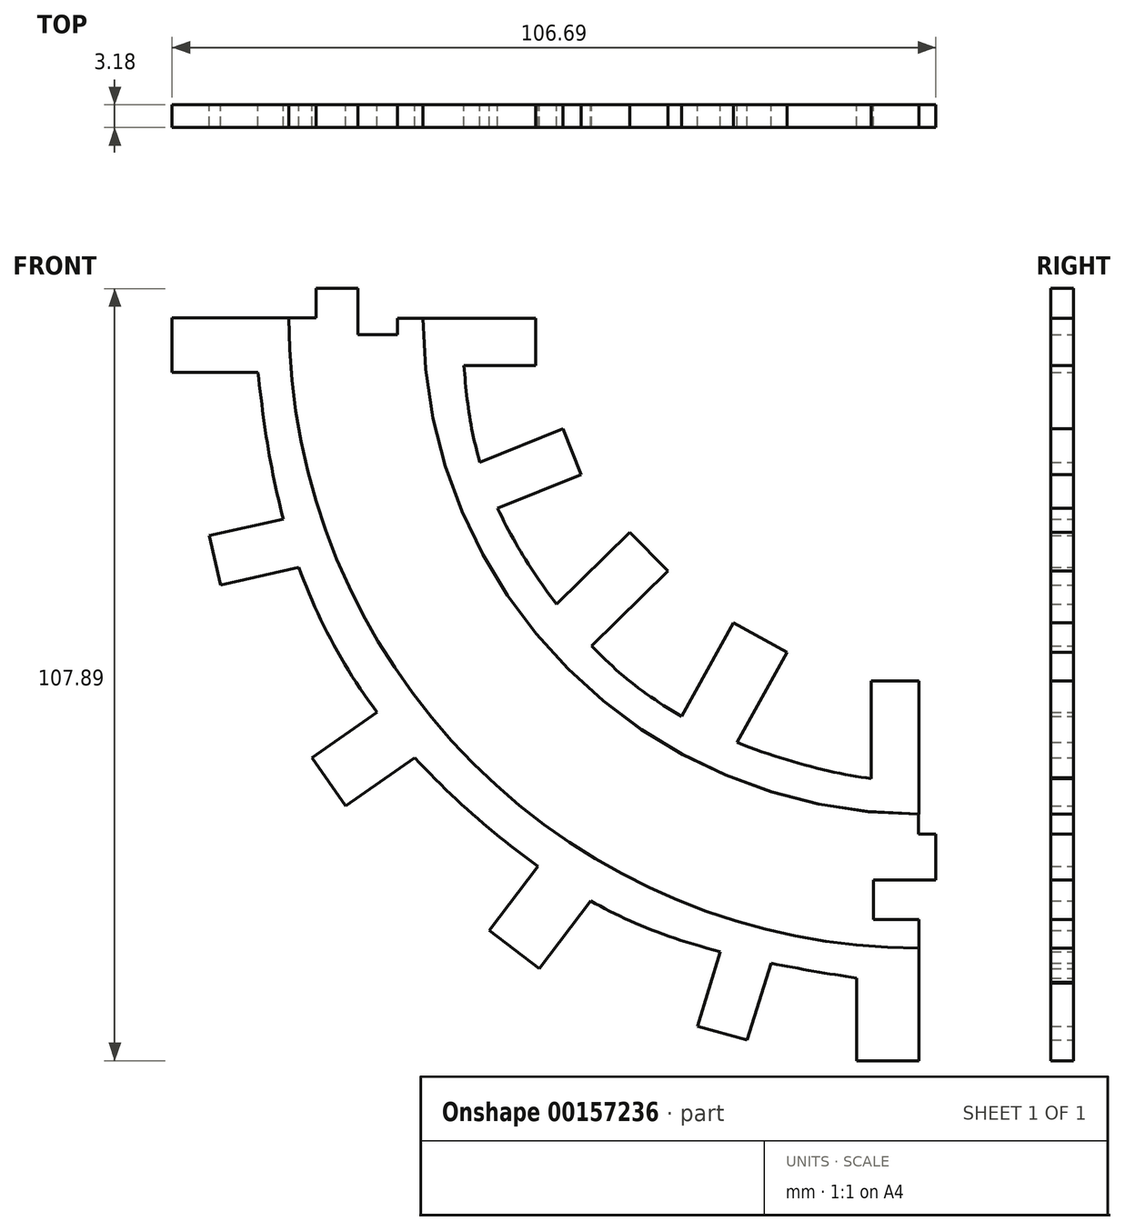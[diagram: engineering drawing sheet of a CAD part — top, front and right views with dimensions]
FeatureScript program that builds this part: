
annotation { "Feature Type Name" : "Feature", "Feature Type Description" : "" }
export const myFeature = defineFeature(function(context is Context, id is Id, definition is map)
    precondition{}
    {
        {
            var Q0;
            Q0=qCreatedBy(makeId("Front.planeOp"),FACE);
            var sketch = newSketch(context, id + "F0", { "sketchPlane" : qUnion([Q0])});
            skArc(sketch, "E0", {"start": v(-92.55, 44.28) * mm, "mid": v(-66.82, -17.99) * mm, "end": v(-4.58, -43.79) * mm});
            skArc(sketch, "E1", {"start": v(-73.85, 44.19) * mm, "mid": v(-53.56, -4.8) * mm, "end": v(-4.58, -25.08) * mm});
            skLineSegment(sketch, "E2", {"start": v(-92.55, 44.28) * mm, "end": v(-108.88, 44.28) * mm});
            skLineSegment(sketch, "E3", {"start": v(-108.88, 44.28) * mm, "end": v(-108.88, 36.69) * mm});
            skLineSegment(sketch, "E4", {"start": v(-108.88, 36.69) * mm, "end": v(-96.88, 36.69) * mm});
            skLineSegment(sketch, "E5", {"start": v(-93.33, 16.17) * mm, "end": v(-103.68, 13.83) * mm});
            skLineSegment(sketch, "E6", {"start": v(-103.68, 13.83) * mm, "end": v(-102.13, 6.96) * mm});
            skLineSegment(sketch, "E7", {"start": v(-102.13, 6.96) * mm, "end": v(-91.2, 9.43) * mm});
            skLineSegment(sketch, "E8", {"start": v(-80.25, -10.86) * mm, "end": v(-89.34, -17.17) * mm});
            skLineSegment(sketch, "E9", {"start": v(-89.34, -17.17) * mm, "end": v(-84.66, -23.9) * mm});
            skLineSegment(sketch, "E10", {"start": v(-84.66, -23.9) * mm, "end": v(-74.97, -17.19) * mm});
            skLineSegment(sketch, "E11", {"start": v(-57.8, -32.34) * mm, "end": v(-64.59, -41.33) * mm});
            skLineSegment(sketch, "E12", {"start": v(-64.59, -41.33) * mm, "end": v(-57.57, -46.63) * mm});
            skLineSegment(sketch, "E13", {"start": v(-57.57, -46.63) * mm, "end": v(-50.43, -37.17) * mm});
            skLineSegment(sketch, "E14", {"start": v(-32.3, -44.28) * mm, "end": v(-35.51, -54.71) * mm});
            skLineSegment(sketch, "E15", {"start": v(-35.51, -54.71) * mm, "end": v(-28.6, -56.6) * mm});
            skLineSegment(sketch, "E16", {"start": v(-13.27, -47.97) * mm, "end": v(-13.27, -59.52) * mm});
            skLineSegment(sketch, "E17", {"start": v(-13.27, -59.52) * mm, "end": v(-4.58, -59.52) * mm});
            skLineSegment(sketch, "E18", {"start": v(-4.58, -59.52) * mm, "end": v(-4.58, -43.79) * mm});
            skLineSegment(sketch, "E19", {"start": v(-73.85, 44.19) * mm, "end": v(-58.08, 44.19) * mm});
            skLineSegment(sketch, "E20", {"start": v(-58.08, 44.19) * mm, "end": v(-58.08, 37.6) * mm});
            skLineSegment(sketch, "E21", {"start": v(-58.08, 37.6) * mm, "end": v(-68.12, 37.6) * mm});
            skLineSegment(sketch, "E22", {"start": v(-28.6, -56.6) * mm, "end": v(-25.18, -45.9) * mm});
            skLineSegment(sketch, "E23", {"start": v(-4.58, -25.08) * mm, "end": v(-4.58, -6.48) * mm});
            skLineSegment(sketch, "E24", {"start": v(-4.58, -6.48) * mm, "end": v(-11.24, -6.48) * mm});
            skLineSegment(sketch, "E25", {"start": v(-11.24, -6.48) * mm, "end": v(-11.24, -20.09) * mm});
            skLineSegment(sketch, "E26", {"start": v(-29.94, -15.04) * mm, "end": v(-22.98, -2.48) * mm});
            skLineSegment(sketch, "E27", {"start": v(-22.98, -2.48) * mm, "end": v(-30.46, 1.66) * mm});
            skLineSegment(sketch, "E28", {"start": v(-30.46, 1.66) * mm, "end": v(-37.7, -11.39) * mm});
            skLineSegment(sketch, "E29", {"start": v(-50.27, -1.57) * mm, "end": v(-39.6, 8.89) * mm});
            skLineSegment(sketch, "E30", {"start": v(-39.6, 8.89) * mm, "end": v(-44.93, 14.34) * mm});
            skLineSegment(sketch, "E31", {"start": v(-44.93, 14.34) * mm, "end": v(-55.2, 4.28) * mm});
            skLineSegment(sketch, "E32", {"start": v(-63.41, 17.66) * mm, "end": v(-51.74, 22.36) * mm});
            skLineSegment(sketch, "E33", {"start": v(-51.74, 22.36) * mm, "end": v(-54.32, 28.76) * mm});
            skLineSegment(sketch, "E34", {"start": v(-54.32, 28.76) * mm, "end": v(-65.88, 24.1) * mm});
            skFitSpline(sketch, "E35", {"points": [v(-97.63, 44.28) * mm, v(-93.33, 16.17) * mm, v(-80.25, -10.86) * mm, v(-57.8, -32.34) * mm, v(-32.3, -44.28) * mm, v(-4.58, -48.7) * mm, v(-4.58, -48.55) * mm], "startDerivative": vector(13.82, -145.43) * mm, "endDerivative": vector(-5.7, 11.68) * mm});
            skFitSpline(sketch, "E36", {"points": [v(-68.46, 44.19) * mm, v(-65.88, 24.1) * mm, v(-55.2, 4.28) * mm, v(-37.7, -11.39) * mm, v(-11.24, -20.09) * mm, v(-4.58, -20.09) * mm, v(-4.58, -19.96) * mm], "startDerivative": vector(4.33, -100.26) * mm, "endDerivative": vector(-3.13, 8.35) * mm});
            skPoint(sketch, "E37.orphan", {"position": v(-53.56, -4.8) * mm});
            skSolve(sketch);
        }
        {
            var Q0;
            Q0 = qSketchRegion(id + "F0", true);
            extrude(context, id + "F1", {"entities" : qUnion([Q0]), "depth" : 3.17 * mm});
        }
        {
            var Q0;
            Q0=qCreatedBy(makeId("Front.planeOp"),FACE);
            var sketch = newSketch(context, id + "F2", { "sketchPlane" : qUnion([Q0])});
            skLineSegment(sketch, "E38", {"start": v(-92.55, 44.28) * mm, "end": v(-88.75, 44.28) * mm});
            skLineSegment(sketch, "E39", {"start": v(-88.75, 44.28) * mm, "end": v(-88.75, 48.37) * mm});
            skLineSegment(sketch, "E40", {"start": v(-88.75, 48.37) * mm, "end": v(-82.93, 48.37) * mm});
            skLineSegment(sketch, "E41", {"start": v(-82.93, 48.37) * mm, "end": v(-82.93, 41.92) * mm});
            skLineSegment(sketch, "E42", {"start": v(-82.93, 41.92) * mm, "end": v(-77.42, 41.92) * mm});
            skLineSegment(sketch, "E43", {"start": v(-77.42, 41.92) * mm, "end": v(-77.42, 44.19) * mm});
            skLineSegment(sketch, "E44", {"start": v(-77.42, 44.19) * mm, "end": v(-73.85, 44.19) * mm});
            skLineSegment(sketch, "E45", {"start": v(-4.58, -43.79) * mm, "end": v(-4.58, -39.8) * mm});
            skLineSegment(sketch, "E46", {"start": v(-4.58, -39.8) * mm, "end": v(-10.94, -39.8) * mm});
            skLineSegment(sketch, "E47", {"start": v(-10.94, -39.8) * mm, "end": v(-10.94, -34.25) * mm});
            skLineSegment(sketch, "E48", {"start": v(-10.94, -34.25) * mm, "end": v(-2.2, -34.25) * mm});
            skLineSegment(sketch, "E49", {"start": v(-2.2, -34.25) * mm, "end": v(-2.2, -27.86) * mm});
            skLineSegment(sketch, "E50", {"start": v(-2.2, -27.86) * mm, "end": v(-4.64, -27.86) * mm});
            skLineSegment(sketch, "E51", {"start": v(-4.64, -27.86) * mm, "end": v(-4.64, -25.08) * mm});
            skArc(sketch, "E52.0", {"start": v(-73.85, 44.19) * mm, "mid": v(-53.56, -4.8) * mm, "end": v(-4.58, -25.08) * mm});
            skArc(sketch, "E53.0", {"start": v(-92.55, 44.28) * mm, "mid": v(-66.82, -17.99) * mm, "end": v(-4.58, -43.79) * mm});
            skSolve(sketch);
        }
        {
            var Q0;
            Q0=makeQuery(id+"F2.imprint","IMPRINT",FACE,{"disambiguationData":[TD([[makeQuery(id+"F2.imprint","IMPRINT",EDGE,{"derivedFrom":sQuery(id+"F2.wireOp",EDGE,"E38")}),-1.0]])]});
            extrude(context, id + "F3", {"entities" : qUnion([Q0]), "depth" : 3.17 * mm});
        }
    });
